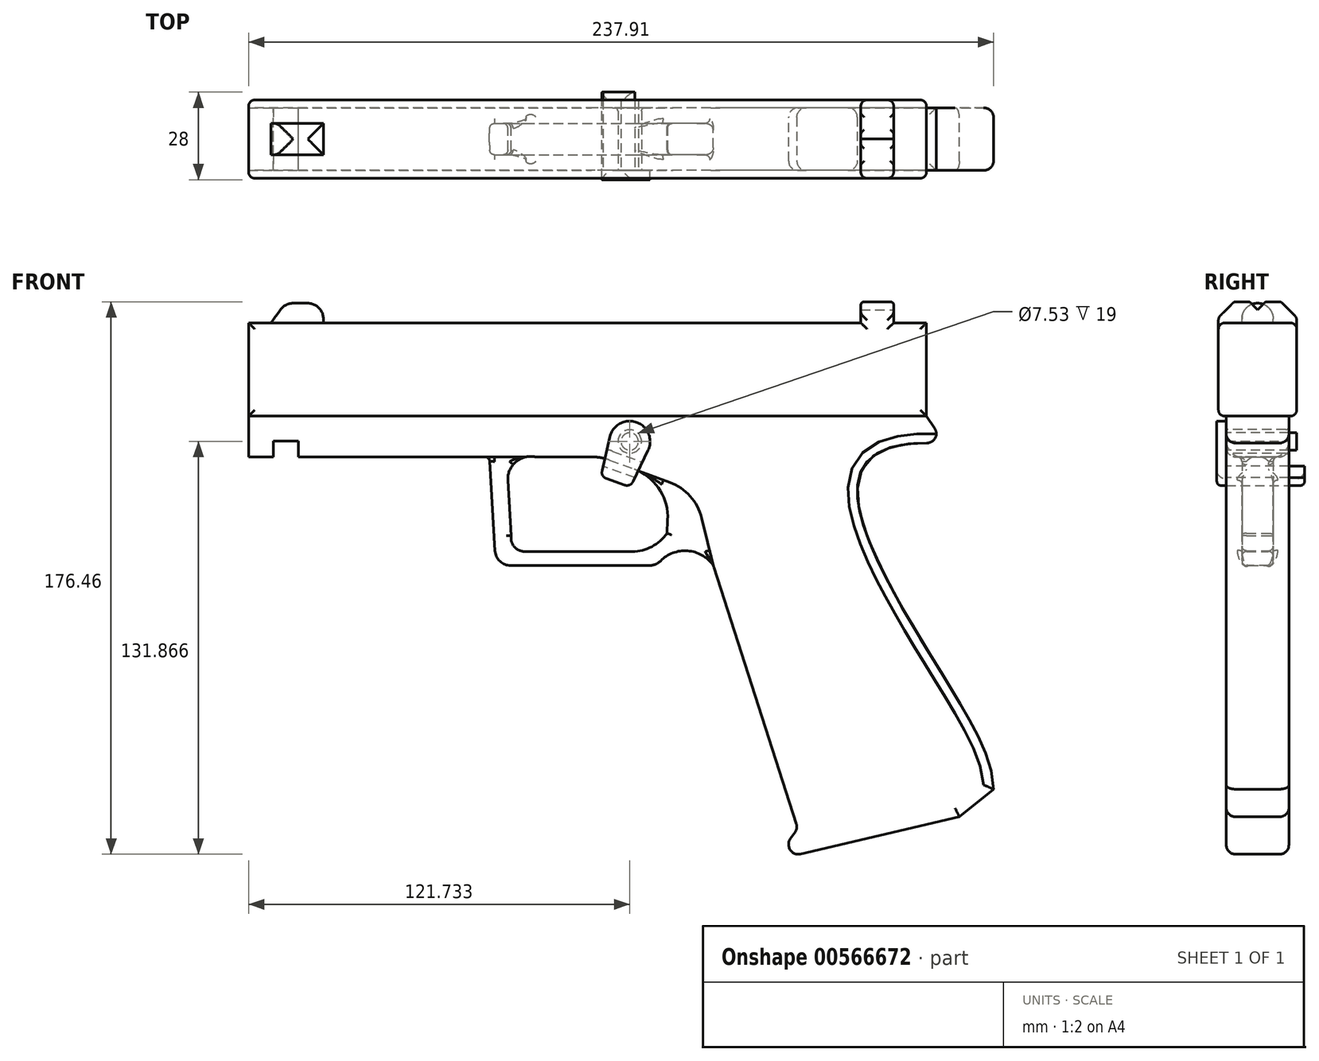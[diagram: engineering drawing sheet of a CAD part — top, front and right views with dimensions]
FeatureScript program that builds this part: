
annotation { "Feature Type Name" : "Feature", "Feature Type Description" : "" }
export const myFeature = defineFeature(function(context is Context, id is Id, definition is map)
    precondition{}
    {
        {
            var Q0;
            Q0=qCreatedBy(makeId("Front.planeOp"),FACE);
            var sketch = newSketch(context, id + "F0", { "sketchPlane" : qUnion([Q0])});
            skLineSegment(sketch, "E0", {"start": v(-104.06, 53.92) * mm, "end": v(91.47, 53.92) * mm});
            skLineSegment(sketch, "E1", {"start": v(91.47, 53.92) * mm, "end": v(91.47, 60.63) * mm});
            skLineSegment(sketch, "E2", {"start": v(91.47, 60.63) * mm, "end": v(101.96, 60.63) * mm});
            skLineSegment(sketch, "E3", {"start": v(101.96, 60.63) * mm, "end": v(101.96, 53.92) * mm});
            skLineSegment(sketch, "E4", {"start": v(101.96, 53.92) * mm, "end": v(112.45, 53.92) * mm});
            skLineSegment(sketch, "E5", {"start": v(112.45, 53.92) * mm, "end": v(112.45, 24.13) * mm});
            skLineSegment(sketch, "E6", {"start": v(112.45, 24.13) * mm, "end": v(-104.06, 24.13) * mm});
            skLineSegment(sketch, "E7", {"start": v(-104.06, 24.13) * mm, "end": v(-104.06, 53.92) * mm});
            skLineSegment(sketch, "E8", {"start": v(-96.93, 53.92) * mm, "end": v(-92.31, 60.21) * mm});
            skLineSegment(sketch, "E9", {"start": v(-92.31, 60.21) * mm, "end": v(-80.14, 60.21) * mm});
            skLineSegment(sketch, "E10", {"start": v(-80.14, 60.21) * mm, "end": v(-80.14, 53.92) * mm});
            skLineSegment(sketch, "E11", {"start": v(112.45, 24.13) * mm, "end": v(118.33, 15.32) * mm});
            skFitSpline(sketch, "E12", {"points": [v(118.33, 15.32) * mm, v(90.63, -3.57) * mm, v(128.4, -77) * mm, v(133.85, -95.04) * mm], "startDerivative": vector(-221.46, 16.71) * mm, "endDerivative": vector(4.64, -61.17) * mm});
            skLineSegment(sketch, "E13", {"start": v(133.85, -95.04) * mm, "end": v(122.94, -103.85) * mm});
            skLineSegment(sketch, "E14", {"start": v(122.94, -103.85) * mm, "end": v(69.23, -116.44) * mm});
            skLineSegment(sketch, "E15", {"start": v(69.23, -116.44) * mm, "end": v(68.17, -111.9) * mm});
            skLineSegment(sketch, "E16", {"start": v(-104.06, 24.13) * mm, "end": v(-104.06, 11.12) * mm});
            skLineSegment(sketch, "E17", {"start": v(-104.06, 11.12) * mm, "end": v(-96.09, 11.12) * mm});
            skLineSegment(sketch, "E18", {"start": v(-96.09, 11.12) * mm, "end": v(-96.09, 16.15) * mm});
            skLineSegment(sketch, "E19", {"start": v(-96.09, 16.15) * mm, "end": v(-88.12, 16.15) * mm});
            skLineSegment(sketch, "E20", {"start": v(-88.12, 16.15) * mm, "end": v(-88.12, 11.12) * mm});
            skLineSegment(sketch, "E21", {"start": v(-88.12, 11.12) * mm, "end": v(5.51, 11.12) * mm});
            skLineSegment(sketch, "E22", {"start": v(11.17, 10.1) * mm, "end": v(19.13, 7.17) * mm});
            skLineSegment(sketch, "E23", {"start": v(40.63, -8.4) * mm, "end": v(44.5, -24.07) * mm});
            skLineSegment(sketch, "E24", {"start": v(68.17, -111.9) * mm, "end": v(71.38, -107.57) * mm});
            skLineSegment(sketch, "E25", {"start": v(71.38, -107.57) * mm, "end": v(44.5, -24.07) * mm});
            skLineSegment(sketch, "E26", {"start": v(-27.13, 11.12) * mm, "end": v(-25.05, -23.6) * mm});
            skLineSegment(sketch, "E27", {"start": v(-25.05, -23.6) * mm, "end": v(26.28, -23.6) * mm});
            skArc(sketch, "E28", {"start": v(44.38, -23.6) * mm, "mid": v(35.33, -18.86) * mm, "end": v(26.28, -23.6) * mm});
            skPoint(sketch, "E29.visualSharp", {"position": v(38.56, 0) * mm});
            skArc(sketch, "E29.filletArc", {"start": v(40.63, -8.4) * mm, "mid": v(36.95, -1.44) * mm, "end": v(30.44, 3) * mm});
            skPoint(sketch, "E30.visualSharp", {"position": v(8.43, 11.12) * mm});
            skArc(sketch, "E30.filletArc", {"start": v(11.17, 10.1) * mm, "mid": v(8.39, 10.86) * mm, "end": v(5.51, 11.12) * mm});
            skLineSegment(sketch, "E31", {"start": v(-21.25, 3.54) * mm, "end": v(-20.2, -14.07) * mm});
            skLineSegment(sketch, "E32", {"start": v(-15.9, -19.1) * mm, "end": v(18.53, -19.1) * mm});
            skLineSegment(sketch, "E33", {"start": v(29.54, -13.29) * mm, "end": v(29.77, -9.04) * mm});
            skArc(sketch, "E34", {"start": v(-20.2, -14.07) * mm, "mid": v(-19.2, -17.58) * mm, "end": v(-15.9, -19.1) * mm});
            skArc(sketch, "E35", {"start": v(-12.53, 11.12) * mm, "mid": v(-18.76, 9.48) * mm, "end": v(-21.25, 3.54) * mm});
            skArc(sketch, "E36", {"start": v(18.53, -19.1) * mm, "mid": v(24.75, -17.56) * mm, "end": v(29.54, -13.29) * mm});
            skPoint(sketch, "E37.visualSharp", {"position": v(30.44, 3) * mm});
            skArc(sketch, "E37.filletArc", {"start": v(29.77, -9.04) * mm, "mid": v(27.12, 0.82) * mm, "end": v(19.13, 7.17) * mm});
            skLineSegment(sketch, "E38", {"start": v(30.44, 3) * mm, "end": v(11.17, 10.1) * mm});
            skSolve(sketch);
        }
        {
            var Q0;
            {var subQ0=sQuery(id+"F0.wireOp",EDGE,"E1");Q0=makeQuery(id+"F0.imprint","IMPRINT",FACE,{"disambiguationData":[TD([[makeQuery(id+"F0.imprint","IMPRINT",EDGE,{"derivedFrom":subQ0}),-1.0]])]});}
            extrude(context, id + "F1", {"entities" : qUnion([Q0]), "endBound" : BoundingType.SYMMETRIC, "depth" : 25 * mm, "offsetDistance" : 25 * mm});
        }
        {
            var Q0;
            Q0=makeQuery(id+"F1.opExtrude","SWEPT_FACE",FACE,{"disambiguationData":[OSD([sQuery(id+"F0.wireOp",EDGE,"E3")])]});
            var sketch = newSketch(context, id + "F2", { "sketchPlane" : qUnion([Q0])});
            skLineSegment(sketch, "E39", {"start": v(-2.5, 60.63) * mm, "end": v(0, 58.13) * mm});
            skLineSegment(sketch, "E40", {"start": v(0, 58.13) * mm, "end": v(2.5, 60.63) * mm});
            skLineSegment(sketch, "E41", {"start": v(-2.5, 60.63) * mm, "end": v(2.5, 60.63) * mm});
            skSolve(sketch);
        }
        {
            var Q0;
            Q0 = qSketchRegion(id + "F2", true);
            extrude(context, id + "F3", {"entities" : qUnion([Q0]), "operationType" : NewBodyOperationType.REMOVE, "endBound" : BoundingType.UP_TO_NEXT, "oppositeDirection" : true, "depth" : 25 * mm, "offsetDistance" : 25 * mm});
        }
        {
            var Q0;
            Q0=makeQuery(id+"F1.opExtrude","CAP_EDGE",EDGE,{"disambiguationData":[OSD([sQuery(id+"F0.wireOp",EDGE,"E2")])],"isStart":false});
            var Q1;
            Q1=makeQuery(id+"F1.opExtrude","CAP_EDGE",EDGE,{"disambiguationData":[OSD([sQuery(id+"F0.wireOp",EDGE,"E2")])],"isStart":true});
            chamfer(context, id + "F4", {"entities" : qUnion([Q0, Q1]), "width" : 5 * mm, "tangentPropagation" : true});
        }
        {
            var Q0;
            Q0=makeQuery(id+"F0.imprint","IMPRINT",FACE,{"disambiguationData":[TD([[makeQuery(id+"F0.imprint","IMPRINT",EDGE,{"derivedFrom":sQuery(id+"F0.wireOp",EDGE,"E6")}),1.0]])]});
            extrude(context, id + "F5", {"entities" : qUnion([Q0]), "operationType" : NewBodyOperationType.ADD, "endBound" : BoundingType.SYMMETRIC, "depth" : 20 * mm, "offsetDistance" : 25 * mm});
        }
        {
            var Q0;
            {var subQ3=sQuery(id+"F0.wireOp",EDGE,"E26");Q0=makeQuery(id+"F0.imprint","IMPRINT",FACE,{"disambiguationData":[TD([[makeQuery(id+"F0.imprint","IMPRINT",EDGE,{"derivedFrom":subQ3}),1.0]])]});}
            var Q1;
            {var subQ0=sQuery(id+"F0.wireOp",EDGE,"E8");Q1=makeQuery(id+"F0.imprint","IMPRINT",FACE,{"disambiguationData":[TD([[makeQuery(id+"F0.imprint","IMPRINT",EDGE,{"derivedFrom":subQ0}),-1.0]])]});}
            extrude(context, id + "F6", {"entities" : qUnion([Q0, Q1]), "operationType" : NewBodyOperationType.ADD, "endBound" : BoundingType.SYMMETRIC, "depth" : 10 * mm, "offsetDistance" : 25 * mm});
        }
        {
            var Q0;
            Q0=makeQuery(id+"F1.opExtrude","CAP_FACE",FACE,{"disambiguationData":[OSD([sQuery(id+"F0.wireOp",EDGE,"E0"),sQuery(id+"F0.wireOp",EDGE,"E1"),sQuery(id+"F0.wireOp",EDGE,"E2"),sQuery(id+"F0.wireOp",EDGE,"E3"),sQuery(id+"F0.wireOp",EDGE,"E4"),sQuery(id+"F0.wireOp",EDGE,"E5"),sQuery(id+"F0.wireOp",EDGE,"E6"),sQuery(id+"F0.wireOp",EDGE,"E7")])],"isStart":false});
            var Q1;
            Q1=makeQuery(id+"F1.opExtrude","CAP_FACE",FACE,{"disambiguationData":[OSD([sQuery(id+"F0.wireOp",EDGE,"E0"),sQuery(id+"F0.wireOp",EDGE,"E1"),sQuery(id+"F0.wireOp",EDGE,"E2"),sQuery(id+"F0.wireOp",EDGE,"E3"),sQuery(id+"F0.wireOp",EDGE,"E4"),sQuery(id+"F0.wireOp",EDGE,"E5"),sQuery(id+"F0.wireOp",EDGE,"E6"),sQuery(id+"F0.wireOp",EDGE,"E7")])],"isStart":true});
            fillet(context, id + "F7", {"entities" : qUnion([Q0, Q1]), "radius" : 2 * mm, "tangentPropagation" : true, "allowEdgeOverflow" : false});
        }
        {
            var Q0;
            Q0=makeQuery(id+"F6.opExtrude","SWEPT_FACE",FACE,{"disambiguationData":[OSD([sQuery(id+"F0.wireOp",EDGE,"E9")])]});
            fillet(context, id + "F8", {"entities" : qUnion([Q0]), "radius" : 5 * mm, "tangentPropagation" : true, "allowEdgeOverflow" : false});
        }
        {
            var Q0;
            Q0=makeQuery(id+"F5.opExtrude","SWEPT_EDGE",EDGE,{"disambiguationData":[OSD([sQuery(id+"F0.wireOp",EDGE,"E11"),sQuery(id+"F0.wireOp",EDGE,"E12")])]});
            var Q1;
            Q1=makeQuery(id+"F5.opExtrude","CAP_EDGE",EDGE,{"disambiguationData":[OSD([sQuery(id+"F0.wireOp",EDGE,"E12")])],"isStart":false});
            var Q2;
            Q2=makeQuery(id+"F5.opExtrude","CAP_EDGE",EDGE,{"disambiguationData":[OSD([sQuery(id+"F0.wireOp",EDGE,"E12")])],"isStart":true});
            var Q3;
            Q3=makeQuery(id+"F5.opExtrude","CAP_EDGE",EDGE,{"disambiguationData":[OSD([sQuery(id+"F0.wireOp",EDGE,"E13")])],"isStart":false});
            var Q4;
            Q4=makeQuery(id+"F5.opExtrude","CAP_EDGE",EDGE,{"disambiguationData":[OSD([sQuery(id+"F0.wireOp",EDGE,"E13")])],"isStart":true});
            var Q5;
            Q5=makeQuery(id+"F5.opExtrude","CAP_EDGE",EDGE,{"disambiguationData":[OSD([sQuery(id+"F0.wireOp",EDGE,"E14")])],"isStart":false});
            var Q6;
            Q6=makeQuery(id+"F5.opExtrude","CAP_EDGE",EDGE,{"disambiguationData":[OSD([sQuery(id+"F0.wireOp",EDGE,"E14")])],"isStart":true});
            var Q7;
            Q7=makeQuery(id+"F5.opExtrude","CAP_EDGE",EDGE,{"disambiguationData":[OSD([sQuery(id+"F0.wireOp",EDGE,"E25")])],"isStart":true});
            var Q8;
            Q8=makeQuery(id+"F5.opExtrude","CAP_EDGE",EDGE,{"disambiguationData":[OSD([sQuery(id+"F0.wireOp",EDGE,"E25")])],"isStart":false});
            var Q9;
            Q9=makeQuery(id+"F5.opExtrude","CAP_EDGE",EDGE,{"disambiguationData":[OSD([sQuery(id+"F0.wireOp",EDGE,"E15")])],"isStart":true});
            var Q10;
            Q10=makeQuery(id+"F5.opExtrude","CAP_EDGE",EDGE,{"disambiguationData":[OSD([sQuery(id+"F0.wireOp",EDGE,"E24")])],"isStart":true});
            var Q11;
            Q11=makeQuery(id+"F5.opExtrude","SWEPT_EDGE",EDGE,{"disambiguationData":[OSD([sQuery(id+"F0.wireOp",EDGE,"E15"),sQuery(id+"F0.wireOp",EDGE,"E24")])]});
            var Q12;
            Q12=makeQuery(id+"F5.opExtrude","SWEPT_FACE",FACE,{"disambiguationData":[OSD([sQuery(id+"F0.wireOp",EDGE,"E24")])]});
            var Q13;
            Q13=makeQuery(id+"F5.opExtrude","SWEPT_FACE",FACE,{"disambiguationData":[OSD([sQuery(id+"F0.wireOp",EDGE,"E15")])]});
            var Q14;
            Q14=makeQuery(id+"F5.opExtrude","SWEPT_FACE",FACE,{"disambiguationData":[OSD([sQuery(id+"F0.wireOp",EDGE,"E25")])]});
            var Q15;
            Q15=makeQuery(id+"F5.opExtrude","CAP_EDGE",EDGE,{"disambiguationData":[OSD([sQuery(id+"F0.wireOp",EDGE,"E23")])],"isStart":true});
            var Q16;
            Q16=makeQuery(id+"F5.opExtrude","CAP_EDGE",EDGE,{"disambiguationData":[OSD([sQuery(id+"F0.wireOp",EDGE,"E29.filletArc")])],"isStart":true});
            var Q17;
            Q17=makeQuery(id+"F5.opExtrude","CAP_EDGE",EDGE,{"disambiguationData":[OSD([sQuery(id+"F0.wireOp",EDGE,"E38")])],"isStart":true});
            var Q18;
            Q18=makeQuery(id+"F5.opExtrude","SWEPT_FACE",FACE,{"disambiguationData":[OSD([sQuery(id+"F0.wireOp",EDGE,"E30.filletArc")])]});
            var Q19;
            {var subQ0=sQuery(id+"F0.wireOp",EDGE,"E21");Q19=makeQuery(id+"F5.opExtrude","SWEPT_FACE",FACE,{"disambiguationData":[OSD([subQ0]),TDD([makeQuery(id+"F0.imprint","IMPRINT",EDGE,{"disambiguationData":[TD([[makeQuery(id+"F0.imprint","INTERSECT",VERTEX,{"derivedFrom":[subQ0,sQuery(id+"F0.wireOp",EDGE,"E30.filletArc")]}),1.0]])],"derivedFrom":subQ0})])]});}
            fillet(context, id + "F9", {"entities" : qUnion([Q0, Q1, Q2, Q3, Q4, Q5, Q6, Q7, Q8, Q9, Q10, Q11, Q12, Q13, Q14, Q15, Q16, Q17, Q18, Q19]), "radius" : 3 * mm, "tangentPropagation" : true, "allowEdgeOverflow" : false});
        }
        {
            var Q0;
            Q0=makeQuery(id+"F6.opExtrude","CAP_FACE",FACE,{"disambiguationData":[OSD([sQuery(id+"F0.wireOp",EDGE,"E21"),sQuery(id+"F0.wireOp",EDGE,"E23"),sQuery(id+"F0.wireOp",EDGE,"E26"),sQuery(id+"F0.wireOp",EDGE,"E27"),sQuery(id+"F0.wireOp",EDGE,"E28"),sQuery(id+"F0.wireOp",EDGE,"E29.filletArc"),sQuery(id+"F0.wireOp",EDGE,"E31"),sQuery(id+"F0.wireOp",EDGE,"E32"),sQuery(id+"F0.wireOp",EDGE,"E33"),sQuery(id+"F0.wireOp",EDGE,"E34"),sQuery(id+"F0.wireOp",EDGE,"E35"),sQuery(id+"F0.wireOp",EDGE,"E36"),sQuery(id+"F0.wireOp",EDGE,"E37.filletArc"),sQuery(id+"F0.wireOp",EDGE,"E38")])],"isStart":true});
            var Q1;
            Q1=makeQuery(id+"F6.opExtrude","CAP_FACE",FACE,{"disambiguationData":[OSD([sQuery(id+"F0.wireOp",EDGE,"E21"),sQuery(id+"F0.wireOp",EDGE,"E23"),sQuery(id+"F0.wireOp",EDGE,"E26"),sQuery(id+"F0.wireOp",EDGE,"E27"),sQuery(id+"F0.wireOp",EDGE,"E28"),sQuery(id+"F0.wireOp",EDGE,"E29.filletArc"),sQuery(id+"F0.wireOp",EDGE,"E31"),sQuery(id+"F0.wireOp",EDGE,"E32"),sQuery(id+"F0.wireOp",EDGE,"E33"),sQuery(id+"F0.wireOp",EDGE,"E34"),sQuery(id+"F0.wireOp",EDGE,"E35"),sQuery(id+"F0.wireOp",EDGE,"E36"),sQuery(id+"F0.wireOp",EDGE,"E37.filletArc"),sQuery(id+"F0.wireOp",EDGE,"E38")])],"isStart":false});
            fillet(context, id + "F10", {"entities" : qUnion([Q0, Q1]), "radius" : 1.5 * mm, "tangentPropagation" : true, "allowEdgeOverflow" : false});
        }
        {
            var Q0;
            Q0=makeQuery(id+"F6.opExtrude","SWEPT_EDGE",EDGE,{"disambiguationData":[OSD([sQuery(id+"F0.wireOp",EDGE,"E26"),sQuery(id+"F0.wireOp",EDGE,"E27")])]});
            var Q1;
            Q1=makeQuery(id+"F6.opExtrude","SWEPT_EDGE",EDGE,{"disambiguationData":[OSD([sQuery(id+"F0.wireOp",EDGE,"E27"),sQuery(id+"F0.wireOp",EDGE,"E28")])]});
            fillet(context, id + "F11", {"entities" : qUnion([Q0, Q1]), "radius" : 5 * mm, "tangentPropagation" : true, "allowEdgeOverflow" : false});
        }
        {
            var Q0;
            Q0=makeQuery(id+"F5.opExtrude","CAP_FACE",FACE,{"disambiguationData":[OSD([sQuery(id+"F0.wireOp",EDGE,"E6"),sQuery(id+"F0.wireOp",EDGE,"E11"),sQuery(id+"F0.wireOp",EDGE,"E12"),sQuery(id+"F0.wireOp",EDGE,"E13"),sQuery(id+"F0.wireOp",EDGE,"E14"),sQuery(id+"F0.wireOp",EDGE,"E15"),sQuery(id+"F0.wireOp",EDGE,"E16"),sQuery(id+"F0.wireOp",EDGE,"E17"),sQuery(id+"F0.wireOp",EDGE,"E18"),sQuery(id+"F0.wireOp",EDGE,"E19"),sQuery(id+"F0.wireOp",EDGE,"E20"),sQuery(id+"F0.wireOp",EDGE,"E21"),sQuery(id+"F0.wireOp",EDGE,"E23"),sQuery(id+"F0.wireOp",EDGE,"E24"),sQuery(id+"F0.wireOp",EDGE,"E25"),sQuery(id+"F0.wireOp",EDGE,"E29.filletArc"),sQuery(id+"F0.wireOp",EDGE,"E30.filletArc"),sQuery(id+"F0.wireOp",EDGE,"E35"),sQuery(id+"F0.wireOp",EDGE,"E38")])],"isStart":false});
            var sketch = newSketch(context, id + "F12", { "sketchPlane" : qUnion([Q0])});
            skCircle(sketch, "E42", {"center": v(17.67, 16.04) * mm, "radius": 3.76 * mm});
            skSolve(sketch);
        }
        {
            var Q0;
            Q0 = qSketchRegion(id + "F12", true);
            extrude(context, id + "F13", {"entities" : qUnion([Q0]), "operationType" : NewBodyOperationType.REMOVE, "oppositeDirection" : true, "depth" : 25 * mm, "offsetDistance" : 25 * mm});
        }
        {
            var Q0;
            Q0=makeQuery(id+"F13.boolean.opBoolean","COPY",EDGE,{"derivedFrom":makeQuery(id+"F13.opExtrude","CAP_EDGE",EDGE,{"disambiguationData":[OSD([sQuery(id+"F12.wireOp",EDGE,"E42")])],"isStart":true})});
            var Q1;
            Q1=makeQuery(id+"F13.boolean.opBoolean","INTERSECT",EDGE,{"derivedFrom":[makeQuery(id+"F5.opExtrude","CAP_FACE",FACE,{"disambiguationData":[OSD([sQuery(id+"F0.wireOp",EDGE,"E6"),sQuery(id+"F0.wireOp",EDGE,"E11"),sQuery(id+"F0.wireOp",EDGE,"E12"),sQuery(id+"F0.wireOp",EDGE,"E13"),sQuery(id+"F0.wireOp",EDGE,"E14"),sQuery(id+"F0.wireOp",EDGE,"E15"),sQuery(id+"F0.wireOp",EDGE,"E16"),sQuery(id+"F0.wireOp",EDGE,"E17"),sQuery(id+"F0.wireOp",EDGE,"E18"),sQuery(id+"F0.wireOp",EDGE,"E19"),sQuery(id+"F0.wireOp",EDGE,"E20"),sQuery(id+"F0.wireOp",EDGE,"E21"),sQuery(id+"F0.wireOp",EDGE,"E23"),sQuery(id+"F0.wireOp",EDGE,"E24"),sQuery(id+"F0.wireOp",EDGE,"E25"),sQuery(id+"F0.wireOp",EDGE,"E29.filletArc"),sQuery(id+"F0.wireOp",EDGE,"E30.filletArc"),sQuery(id+"F0.wireOp",EDGE,"E35"),sQuery(id+"F0.wireOp",EDGE,"E38")])],"isStart":true}),makeQuery(id+"F13.opExtrude","SWEPT_FACE",FACE,{"disambiguationData":[OSD([sQuery(id+"F12.wireOp",EDGE,"E42")])]})]});
            fillet(context, id + "F14", {"entities" : qUnion([Q0, Q1]), "radius" : 1 * mm, "tangentPropagation" : true, "allowEdgeOverflow" : false});
        }
        {
            var Q0;
            {var subQ1=sQuery(id+"F0.wireOp",EDGE,"E2");Q0=makeQuery(id+"F3.boolean.opBoolean","SPLIT",FACE,{"disambiguationData":[TD([makeQuery(id+"F3.opExtrude","SWEPT_FACE",FACE,{"disambiguationData":[OSD([sQuery(id+"F2.wireOp",EDGE,"E39")])]})])],"derivedFrom":makeQuery(id+"F1.opExtrude","SWEPT_FACE",FACE,{"disambiguationData":[OSD([subQ1])]})});}
            var Q1;
            {var subQ1=sQuery(id+"F0.wireOp",EDGE,"E2");Q1=makeQuery(id+"F3.boolean.opBoolean","SPLIT",FACE,{"disambiguationData":[TD([makeQuery(id+"F3.opExtrude","SWEPT_FACE",FACE,{"disambiguationData":[OSD([sQuery(id+"F2.wireOp",EDGE,"E40")])]})])],"derivedFrom":makeQuery(id+"F1.opExtrude","SWEPT_FACE",FACE,{"disambiguationData":[OSD([subQ1])]})});}
            fillet(context, id + "F15", {"entities" : qUnion([Q0, Q1]), "radius" : 1 * mm, "tangentPropagation" : true, "allowEdgeOverflow" : false});
        }
        {
            var Q0;
            Q0=makeQuery(id+"F5.opExtrude","CAP_EDGE",EDGE,{"disambiguationData":[OSD([sQuery(id+"F0.wireOp",EDGE,"E17")])],"isStart":false});
            var Q1;
            Q1=makeQuery(id+"F5.opExtrude","CAP_EDGE",EDGE,{"disambiguationData":[OSD([sQuery(id+"F0.wireOp",EDGE,"E17")])],"isStart":true});
            fillet(context, id + "F16", {"entities" : qUnion([Q0, Q1]), "radius" : 5 * mm, "tangentPropagation" : true, "allowEdgeOverflow" : false});
        }
        {
            var Q0;
            Q0=makeQuery(id+"F1.opExtrude","CAP_FACE",FACE,{"disambiguationData":[OSD([sQuery(id+"F0.wireOp",EDGE,"E0"),sQuery(id+"F0.wireOp",EDGE,"E1"),sQuery(id+"F0.wireOp",EDGE,"E2"),sQuery(id+"F0.wireOp",EDGE,"E3"),sQuery(id+"F0.wireOp",EDGE,"E4"),sQuery(id+"F0.wireOp",EDGE,"E5"),sQuery(id+"F0.wireOp",EDGE,"E6"),sQuery(id+"F0.wireOp",EDGE,"E7")])],"isStart":false});
            var sketch = newSketch(context, id + "F17", { "sketchPlane" : qUnion([Q0])});
            skCircle(sketch, "E43.0", {"center": v(17.67, 16.04) * mm, "radius": 3.76 * mm, "construction": true});
            skCircle(sketch, "E44", {"center": v(17.67, 16.04) * mm, "radius": 2.76 * mm});
            skSolve(sketch);
        }
        {
            var Q0;
            Q0 = qSketchRegion(id + "F17", true);
            extrude(context, id + "F18", {"entities" : qUnion([Q0]), "oppositeDirection" : true, "depth" : 25 * mm, "offsetDistance" : 25 * mm});
        }
        {
            var Q0;
            Q0=makeQuery(id+"F5.opExtrude","CAP_FACE",FACE,{"disambiguationData":[OSD([sQuery(id+"F0.wireOp",EDGE,"E6"),sQuery(id+"F0.wireOp",EDGE,"E11"),sQuery(id+"F0.wireOp",EDGE,"E12"),sQuery(id+"F0.wireOp",EDGE,"E13"),sQuery(id+"F0.wireOp",EDGE,"E14"),sQuery(id+"F0.wireOp",EDGE,"E15"),sQuery(id+"F0.wireOp",EDGE,"E16"),sQuery(id+"F0.wireOp",EDGE,"E17"),sQuery(id+"F0.wireOp",EDGE,"E18"),sQuery(id+"F0.wireOp",EDGE,"E19"),sQuery(id+"F0.wireOp",EDGE,"E20"),sQuery(id+"F0.wireOp",EDGE,"E21"),sQuery(id+"F0.wireOp",EDGE,"E23"),sQuery(id+"F0.wireOp",EDGE,"E24"),sQuery(id+"F0.wireOp",EDGE,"E25"),sQuery(id+"F0.wireOp",EDGE,"E29.filletArc"),sQuery(id+"F0.wireOp",EDGE,"E30.filletArc"),sQuery(id+"F0.wireOp",EDGE,"E35"),sQuery(id+"F0.wireOp",EDGE,"E38")])],"isStart":false});
            var sketch = newSketch(context, id + "F19", { "sketchPlane" : qUnion([Q0])});
            skCircle(sketch, "E45.0.0", {"center": v(17.67, 16.04) * mm, "radius": 2.76 * mm, "construction": true});
            skCircle(sketch, "E46", {"center": v(17.67, 16.04) * mm, "radius": 6.5 * mm});
            skLineSegment(sketch, "E47", {"start": v(11.34, 17.49) * mm, "end": v(8.44, 4.81) * mm});
            skLineSegment(sketch, "E48", {"start": v(8.44, 4.81) * mm, "end": v(17.87, 1.5) * mm});
            skLineSegment(sketch, "E49", {"start": v(17.87, 1.5) * mm, "end": v(23.53, 13.21) * mm});
            skSolve(sketch);
        }
        {
            var Q0;
            Q0 = qSketchRegion(id + "F19", true);
            extrude(context, id + "F20", {"entities" : qUnion([Q0]), "operationType" : NewBodyOperationType.ADD, "depth" : 3 * mm, "offsetDistance" : 25 * mm});
        }
        {
            var Q0;
            {var subQ1=sQuery(id+"F19.wireOp",EDGE,"E48");Q0=makeQuery(id+"F19.imprint","IMPRINT",FACE,{"disambiguationData":[TD([[makeQuery(id+"F19.imprint","IMPRINT",EDGE,{"derivedFrom":subQ1}),1.0]])]});}
            var sketch = newSketch(context, id + "F21", { "sketchPlane" : qUnion([Q0])});
            skLineSegment(sketch, "E50.0.2", {"start": v(9.2, 8.11) * mm, "end": v(8.44, 4.81) * mm});
            skLineSegment(sketch, "E50.0.3", {"start": v(8.44, 4.81) * mm, "end": v(17.87, 1.5) * mm});
            skLineSegment(sketch, "E50.0.4", {"start": v(17.87, 1.5) * mm, "end": v(19.35, 4.55) * mm});
            skLineSegment(sketch, "E51", {"start": v(19.35, 4.55) * mm, "end": v(9.2, 8.11) * mm});
            skPoint(sketch, "E50.0.1.start.orphan", {"position": v(10.42, 13.49) * mm});
            skPoint(sketch, "E50.0.0.end.orphan", {"position": v(11.9, 13.03) * mm});
            skPoint(sketch, "E50.0.5.end.orphan", {"position": v(21.7, 9.42) * mm});
            skPoint(sketch, "E50.0.5.start.orphan", {"position": v(20.1, 10) * mm});
            skSolve(sketch);
        }
        {
            var Q0;
            Q0 = qSketchRegion(id + "F21", true);
            extrude(context, id + "F22", {"entities" : qUnion([Q0]), "operationType" : NewBodyOperationType.ADD, "oppositeDirection" : true, "depth" : 25 * mm, "offsetDistance" : 25 * mm});
        }
        {
            var Q0;
            Q0=makeQuery(id+"F22.boolean.opBoolean","MERGE",FACE,{"derivedFrom":[makeQuery(id+"F20.opExtrude","SWEPT_FACE",FACE,{"disambiguationData":[OSD([sQuery(id+"F19.wireOp",EDGE,"E48")])]}),makeQuery(id+"F22.opExtrude","SWEPT_FACE",FACE,{"disambiguationData":[OSD([sQuery(id+"F21.wireOp",EDGE,"E50.0.3")])]})]});
            fillet(context, id + "F23", {"entities" : qUnion([Q0]), "radius" : 2 * mm, "tangentPropagation" : true, "allowEdgeOverflow" : false});
        }
    });
